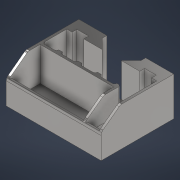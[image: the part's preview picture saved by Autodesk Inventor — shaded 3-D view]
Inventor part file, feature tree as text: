
AUTODESK INVENTOR PART (.ipt)
format: ipt  version: 2022 (Build 260153000, 153)  size: 498,688 bytes
history: native  units: in
note: dims shown in document units (in); Inventor stores cm internally (conversion verified against a paired STEP export)
features: extrude x7, sketch x7, projected_geometry x4, fillet x2, plane x1, mirror x1, chamfer x1, pattern_linear x1
ambient origin geometry x8: Origin, YZ Plane, XZ Plane, XY Plane, X Axis, Y Axis, Z Axis, Center Point
bodies: Solid1 (feature_tree)
feature tree (24):
  extrude  "Extrusion1"  Depth=0.005in
  extrude  "Extrusion2"  Depth=0.125in TaperAngle=0.0deg
  plane  "Work Plane1"
  extrude  "Extrusion3"  Depth=0.0625in TaperAngle=0.0deg
  mirror  "Mirror1"
  extrude  "Extrusion4"  Depth=0.5in TaperAngle=0.0deg
  extrude  "Extrusion7"  Depth=1.9in
  extrude  "Extrusion8"  Depth=1.0in TaperAngle=0.0deg
  chamfer  "Chamfer2"  Distance=5.0in
  fillet  "Fillet1"  Radius=0.25in
  extrude  "Extrusion9"  Depth=0.125in
  pattern_linear  "Rectangular Pattern1"  Spacing1=0.1in  [1 undecoded]
  fillet  "Fillet2"  Radius=0.06in
  sketch  "Sketch1"  dims[d0=1.0in d1=0.0in d2=0.005in]
  sketch  "Sketch3"  dims[d3=1.5in d4=0.125in d5=0.0in]
  sketch  "Sketch4"  dims[d6=0.5in d7=0.0625in d8=0.0in]
  projected_geometry  "Projected Loop1"
  sketch  "Sketch5"  dims[d9=0.0625in d10=0.5in d11=0.0in]
  sketch  "Sketch8"  dims[d24=0.75in d25=1.9in]
  projected_geometry  "Projected Loop2"
  sketch  "Sketch9"  dims[d26=0.06in d27=1.0in d28=0.0in]
  projected_geometry  "Projected Loop3"
  sketch  "Sketch10"  dims[d29=1.0in d30=5.0in d31=0.0in d32=0.25in d33=0.125in d34=45.0deg d35=0.125in d36=0.1in d37=0.06in d38=0.0in d39=1.5748in d41=0.5in d42=0.06in]
  projected_geometry  "Projected Loop4"
note: 1 required parameter value undecoded (feature->parameter linkage not recoverable at this tier; creation-order binding heuristic only, values carry confidence <= 0.55)
